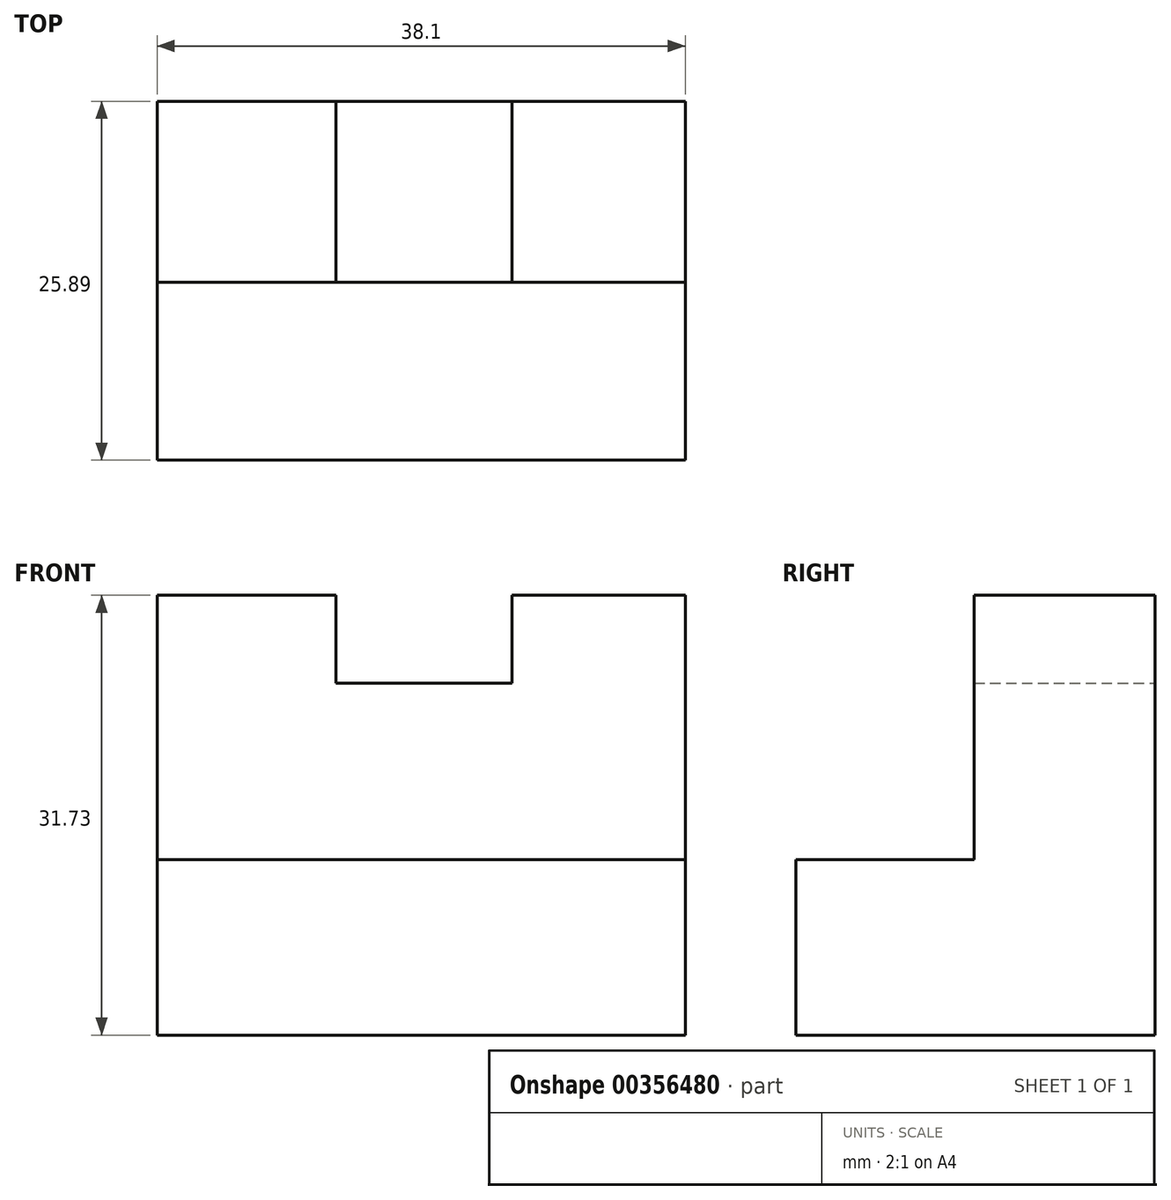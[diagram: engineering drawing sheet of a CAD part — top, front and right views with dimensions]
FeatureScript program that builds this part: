
annotation { "Feature Type Name" : "Feature", "Feature Type Description" : "" }
export const myFeature = defineFeature(function(context is Context, id is Id, definition is map)
    precondition{}
    {
        {
            var Q0;
            Q0=qCreatedBy(makeId("Right.planeOp"),FACE);
            var sketch = newSketch(context, id + "F0", { "sketchPlane" : qUnion([Q0])});
            skLineSegment(sketch, "E0", {"start": v(-30.17, 0) * mm, "end": v(-30.17, 12.65) * mm});
            skLineSegment(sketch, "E1", {"start": v(-30.17, 12.65) * mm, "end": v(-17.33, 12.65) * mm});
            skLineSegment(sketch, "E2", {"start": v(-17.33, 12.65) * mm, "end": v(-17.33, 31.73) * mm});
            skLineSegment(sketch, "E3", {"start": v(-17.33, 31.73) * mm, "end": v(-4.28, 31.73) * mm});
            skLineSegment(sketch, "E4", {"start": v(-4.28, 31.73) * mm, "end": v(-4.28, 0) * mm});
            skLineSegment(sketch, "E5", {"start": v(-30.17, 0) * mm, "end": v(-4.28, 0) * mm});
            skSolve(sketch);
        }
        {
            var Q0;
            Q0 = qSketchRegion(id + "F0", true);
            extrude(context, id + "F1", {"entities" : qUnion([Q0]), "depth" : 38.1 * mm});
        }
        {
            var Q0;
            Q0=makeQuery(id+"F1.opExtrude","SWEPT_FACE",FACE,{"disambiguationData":[OSD([sQuery(id+"F0.wireOp",EDGE,"E3")])]});
            var sketch = newSketch(context, id + "F2", { "sketchPlane" : qUnion([Q0])});
            skLineSegment(sketch, "E6", {"start": v(0, -17.33) * mm, "end": v(12.92, -17.33) * mm});
            skLineSegment(sketch, "E7", {"start": v(12.92, -17.33) * mm, "end": v(12.92, -4.28) * mm});
            skLineSegment(sketch, "E8", {"start": v(12.92, -17.33) * mm, "end": v(25.62, -17.33) * mm});
            skLineSegment(sketch, "E9", {"start": v(25.62, -17.33) * mm, "end": v(25.62, -4.28) * mm});
            skLineSegment(sketch, "E10", {"start": v(70.33, 3.63) * mm, "end": v(67.28, -14.76) * mm});
            skLineSegment(sketch, "E11", {"start": v(68.85, 34.73) * mm, "end": v(75.14, 32.63) * mm});
            skLineSegment(sketch, "E12", {"start": v(12.92, -4.28) * mm, "end": v(25.62, -4.28) * mm});
            skSolve(sketch);
        }
        {
            var Q0;
            Q0 = qSketchRegion(id + "F2", true);
            extrude(context, id + "F3", {"entities" : qUnion([Q0]), "operationType" : NewBodyOperationType.REMOVE, "oppositeDirection" : true, "depth" : 6.35 * mm});
        }
    });
